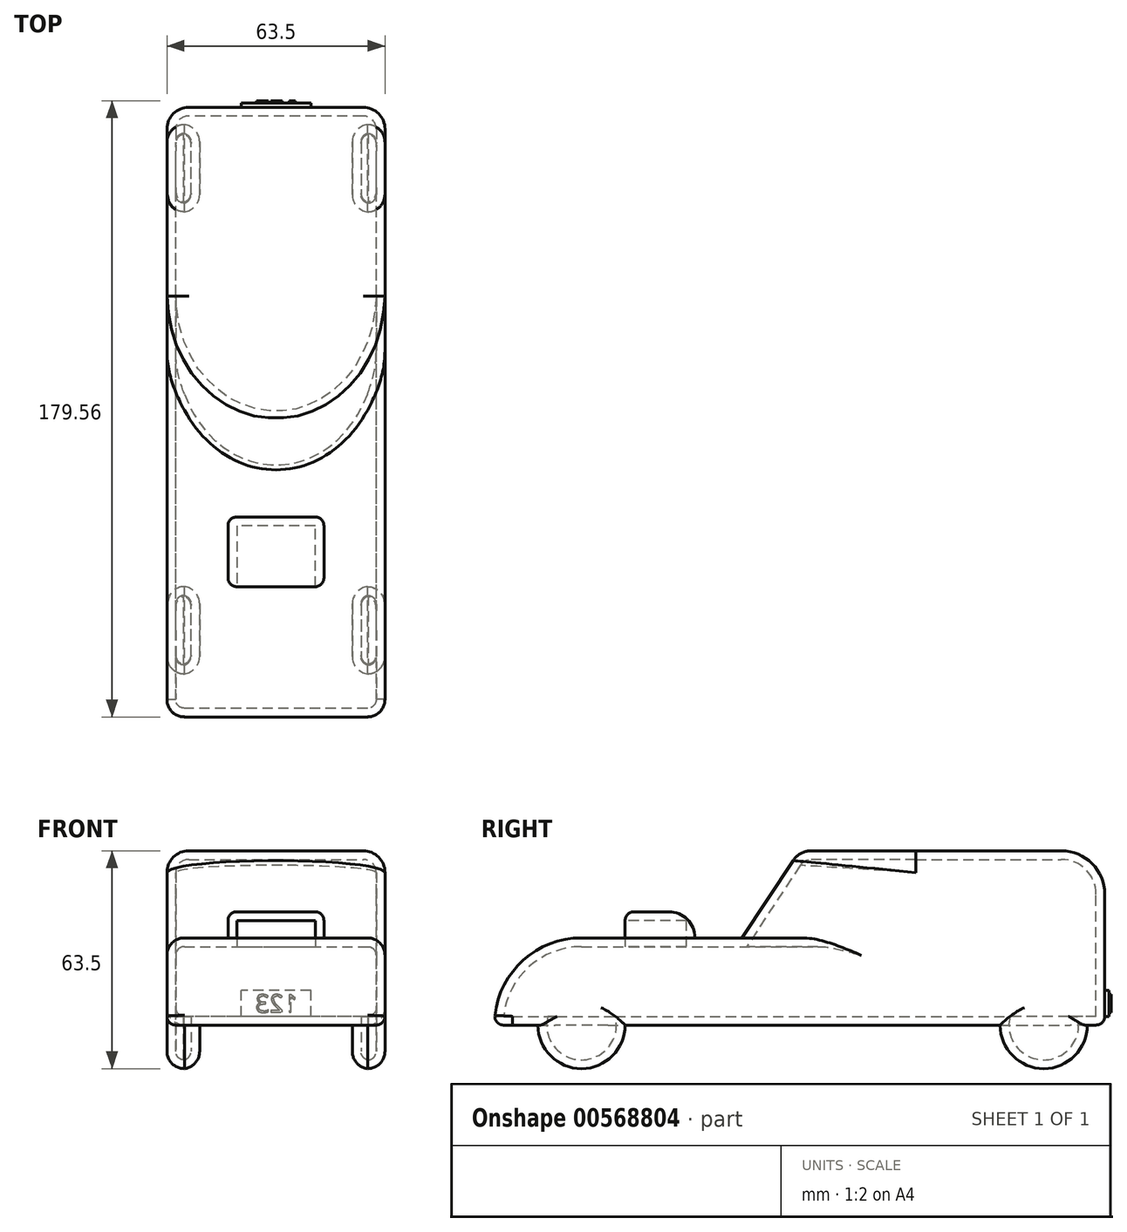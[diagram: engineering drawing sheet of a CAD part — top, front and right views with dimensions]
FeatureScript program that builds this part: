
annotation { "Feature Type Name" : "Feature", "Feature Type Description" : "" }
export const myFeature = defineFeature(function(context is Context, id is Id, definition is map)
    precondition{}
    {
        {
            var Q0;
            Q0=qCreatedBy(makeId("Right.planeOp"),FACE);
            var sketch = newSketch(context, id + "F0", { "sketchPlane" : qUnion([Q0])});
            skLineSegment(sketch, "E0", {"start": v(57.12, 17.31) * mm, "end": v(57.12, -33.49) * mm});
            skLineSegment(sketch, "E1", {"start": v(57.12, -33.49) * mm, "end": v(-69.88, -33.49) * mm});
            skLineSegment(sketch, "E2", {"start": v(-69.88, -33.49) * mm, "end": v(-69.88, -8.09) * mm});
            skLineSegment(sketch, "E3", {"start": v(-69.88, -8.09) * mm, "end": v(2.26, -8.09) * mm});
            skLineSegment(sketch, "E4", {"start": v(2.26, -8.09) * mm, "end": v(19.02, 17.31) * mm});
            skLineSegment(sketch, "E5", {"start": v(19.02, 17.31) * mm, "end": v(57.12, 17.31) * mm});
            skSolve(sketch);
        }
        {
            var Q0;
            Q0 = qSketchRegion(id + "F0", true);
            extrude(context, id + "F1", {"entities" : qUnion([Q0]), "depth" : 63.5 * mm, "offsetDistance" : 25.4 * mm});
        }
        {
            var Q0;
            Q0=makeQuery(id+"F1.opExtrude","CAP_EDGE",EDGE,{"disambiguationData":[OSD([sQuery(id+"F0.wireOp",EDGE,"E4")])],"isStart":true});
            fillet(context, id + "F2", {"entities" : qUnion([Q0]), "radius" : 31.75 * mm, "tangentPropagation" : true, "allowEdgeOverflow" : false});
        }
        {
            var Q0;
            Q0=makeQuery(id+"F1.opExtrude","CAP_EDGE",EDGE,{"disambiguationData":[OSD([sQuery(id+"F0.wireOp",EDGE,"E4")])],"isStart":false});
            fillet(context, id + "F3", {"entities" : qUnion([Q0]), "radius" : 31.75 * mm, "tangentPropagation" : true, "allowEdgeOverflow" : false});
        }
        {
            var Q0;
            Q0=makeQuery(id+"F1.opExtrude","SWEPT_EDGE",EDGE,{"disambiguationData":[OSD([sQuery(id+"F0.wireOp",EDGE,"E2"),sQuery(id+"F0.wireOp",EDGE,"E3")])]});
            fillet(context, id + "F4", {"entities" : qUnion([Q0]), "radius" : 25.4 * mm, "tangentPropagation" : true, "allowEdgeOverflow" : false});
        }
        {
            var Q0;
            Q0=makeQuery(id+"F1.opExtrude","CAP_EDGE",EDGE,{"disambiguationData":[OSD([sQuery(id+"F0.wireOp",EDGE,"E3")])],"isStart":true});
            fillet(context, id + "F5", {"entities" : qUnion([Q0]), "radius" : 5.08 * mm, "tangentPropagation" : true, "allowEdgeOverflow" : false});
        }
        {
            var Q0;
            Q0=makeQuery(id+"F1.opExtrude","CAP_EDGE",EDGE,{"disambiguationData":[OSD([sQuery(id+"F0.wireOp",EDGE,"E3")])],"isStart":false});
            fillet(context, id + "F6", {"entities" : qUnion([Q0]), "radius" : 5.08 * mm, "tangentPropagation" : true, "allowEdgeOverflow" : false});
        }
        {
            var Q0;
            Q0=makeQuery(id+"F1.opExtrude","SWEPT_FACE",FACE,{"disambiguationData":[OSD([sQuery(id+"F0.wireOp",EDGE,"E0")])]});
            extrude(context, id + "F7", {"entities" : qUnion([Q0]), "operationType" : NewBodyOperationType.ADD, "depth" : 50.8 * mm, "offsetDistance" : 25.4 * mm});
        }
        {
            var Q0;
            Q0=makeQuery(id+"F7.opExtrude","CAP_EDGE",EDGE,{"disambiguationData":[OSD([sQuery(id+"F0.wireOp",EDGE,"E0"),sQuery(id+"F0.wireOp",EDGE,"E5")])],"isStart":false});
            fillet(context, id + "F8", {"entities" : qUnion([Q0]), "radius" : 12.7 * mm, "tangentPropagation" : true, "allowEdgeOverflow" : false});
        }
        {
            var Q0;
            {var subQ0=sQuery(id+"F0.wireOp",EDGE,"E0");Q0=makeQuery(id+"F7.boolean.opBoolean","MERGE",FACE,{"derivedFrom":[makeQuery(id+"F1.opExtrude","CAP_FACE",FACE,{"disambiguationData":[OSD([subQ0,sQuery(id+"F0.wireOp",EDGE,"E1"),sQuery(id+"F0.wireOp",EDGE,"E2"),sQuery(id+"F0.wireOp",EDGE,"E3"),sQuery(id+"F0.wireOp",EDGE,"E4"),sQuery(id+"F0.wireOp",EDGE,"E5")])],"isStart":true}),makeQuery(id+"F7.opExtrude","SWEPT_FACE",FACE,{"disambiguationData":[OSD([subQ0]),TDD([makeQuery(id+"F1.opExtrude","CAP_EDGE",EDGE,{"disambiguationData":[OSD([subQ0])],"isStart":true})])]})]});}
            var sketch = newSketch(context, id + "F9", { "sketchPlane" : qUnion([Q0])});
            skCircle(sketch, "E6", {"center": v(-90.14, -33.49) * mm, "radius": 12.7 * mm});
            skCircle(sketch, "E7", {"center": v(44.48, -33.49) * mm, "radius": 12.7 * mm});
            skSolve(sketch);
        }
        {
            var Q0;
            {var subQ0=sQuery(id+"F9.wireOp",EDGE,"E6");var subQ1=sQuery(id+"F0.wireOp",EDGE,"E1");var subQ2=sQuery(id+"F0.wireOp",EDGE,"E0");var subQ3=makeQuery(id+"F7.boolean.opBoolean","MERGE",EDGE,{"derivedFrom":[makeQuery(id+"F1.opExtrude","CAP_EDGE",EDGE,{"disambiguationData":[OSD([subQ1])],"isStart":true}),makeQuery(id+"F7.opExtrude","SWEPT_EDGE",EDGE,{"disambiguationData":[OSD([subQ2,subQ1]),TDD([makeQuery(id+"F1.opExtrude","CAP_VERTEX",VERTEX,{"disambiguationData":[OSD([subQ2,subQ1])],"isStart":true})])]})]});var subQ4=makeQuery(id+"F9.imprint","INTERSECT",VERTEX,{"disambiguationData":[OD(0.0)],"derivedFrom":[subQ3,subQ0]});Q0=makeQuery(id+"F9.imprint","IMPRINT",FACE,{"disambiguationData":[TD([[makeQuery(id+"F9.imprint","IMPRINT",EDGE,{"disambiguationData":[TD([[subQ4,-1.0]])],"derivedFrom":subQ0}),1.0]])]});}
            var Q1;
            {var subQ0=sQuery(id+"F9.wireOp",EDGE,"E6");var subQ1=sQuery(id+"F0.wireOp",EDGE,"E1");var subQ2=sQuery(id+"F0.wireOp",EDGE,"E0");var subQ3=makeQuery(id+"F7.boolean.opBoolean","MERGE",EDGE,{"derivedFrom":[makeQuery(id+"F1.opExtrude","CAP_EDGE",EDGE,{"disambiguationData":[OSD([subQ1])],"isStart":true}),makeQuery(id+"F7.opExtrude","SWEPT_EDGE",EDGE,{"disambiguationData":[OSD([subQ2,subQ1]),TDD([makeQuery(id+"F1.opExtrude","CAP_VERTEX",VERTEX,{"disambiguationData":[OSD([subQ2,subQ1])],"isStart":true})])]})]});var subQ4=makeQuery(id+"F9.imprint","INTERSECT",VERTEX,{"disambiguationData":[OD(0.0)],"derivedFrom":[subQ3,subQ0]});Q1=makeQuery(id+"F9.imprint","IMPRINT",FACE,{"disambiguationData":[TD([[makeQuery(id+"F9.imprint","IMPRINT",EDGE,{"disambiguationData":[TD([[subQ4,1.0]])],"derivedFrom":subQ0}),1.0]])]});}
            var Q2;
            {var subQ0=sQuery(id+"F9.wireOp",EDGE,"E7");var subQ1=sQuery(id+"F0.wireOp",EDGE,"E1");var subQ2=sQuery(id+"F0.wireOp",EDGE,"E0");var subQ3=makeQuery(id+"F7.boolean.opBoolean","MERGE",EDGE,{"derivedFrom":[makeQuery(id+"F1.opExtrude","CAP_EDGE",EDGE,{"disambiguationData":[OSD([subQ1])],"isStart":true}),makeQuery(id+"F7.opExtrude","SWEPT_EDGE",EDGE,{"disambiguationData":[OSD([subQ2,subQ1]),TDD([makeQuery(id+"F1.opExtrude","CAP_VERTEX",VERTEX,{"disambiguationData":[OSD([subQ2,subQ1])],"isStart":true})])]})]});var subQ4=makeQuery(id+"F9.imprint","INTERSECT",VERTEX,{"disambiguationData":[OD(0.0)],"derivedFrom":[subQ3,subQ0]});Q2=makeQuery(id+"F9.imprint","IMPRINT",FACE,{"disambiguationData":[TD([[makeQuery(id+"F9.imprint","IMPRINT",EDGE,{"disambiguationData":[TD([[subQ4,-1.0]])],"derivedFrom":subQ0}),1.0]])]});}
            var Q3;
            {var subQ0=sQuery(id+"F9.wireOp",EDGE,"E7");var subQ1=sQuery(id+"F0.wireOp",EDGE,"E1");var subQ2=sQuery(id+"F0.wireOp",EDGE,"E0");var subQ3=makeQuery(id+"F7.boolean.opBoolean","MERGE",EDGE,{"derivedFrom":[makeQuery(id+"F1.opExtrude","CAP_EDGE",EDGE,{"disambiguationData":[OSD([subQ1])],"isStart":true}),makeQuery(id+"F7.opExtrude","SWEPT_EDGE",EDGE,{"disambiguationData":[OSD([subQ2,subQ1]),TDD([makeQuery(id+"F1.opExtrude","CAP_VERTEX",VERTEX,{"disambiguationData":[OSD([subQ2,subQ1])],"isStart":true})])]})]});var subQ4=makeQuery(id+"F9.imprint","INTERSECT",VERTEX,{"disambiguationData":[OD(0.0)],"derivedFrom":[subQ3,subQ0]});Q3=makeQuery(id+"F9.imprint","IMPRINT",FACE,{"disambiguationData":[TD([[makeQuery(id+"F9.imprint","IMPRINT",EDGE,{"disambiguationData":[TD([[subQ4,1.0]])],"derivedFrom":subQ0}),1.0]])]});}
            extrude(context, id + "F10", {"entities" : qUnion([Q0, Q1, Q2, Q3]), "operationType" : NewBodyOperationType.ADD, "oppositeDirection" : true, "depth" : 9.52 * mm, "offsetDistance" : 25.4 * mm});
        }
        {
            var Q0;
            {var subQ0=sQuery(id+"F0.wireOp",EDGE,"E0");Q0=makeQuery(id+"F7.boolean.opBoolean","MERGE",FACE,{"derivedFrom":[makeQuery(id+"F1.opExtrude","CAP_FACE",FACE,{"disambiguationData":[OSD([subQ0,sQuery(id+"F0.wireOp",EDGE,"E1"),sQuery(id+"F0.wireOp",EDGE,"E2"),sQuery(id+"F0.wireOp",EDGE,"E3"),sQuery(id+"F0.wireOp",EDGE,"E4"),sQuery(id+"F0.wireOp",EDGE,"E5")])],"isStart":false}),makeQuery(id+"F7.opExtrude","SWEPT_FACE",FACE,{"disambiguationData":[OSD([subQ0]),TDD([makeQuery(id+"F1.opExtrude","CAP_EDGE",EDGE,{"disambiguationData":[OSD([subQ0])],"isStart":false})])]})]});}
            var sketch = newSketch(context, id + "F11", { "sketchPlane" : qUnion([Q0])});
            skCircle(sketch, "E8", {"center": v(-44.48, -33.49) * mm, "radius": 12.7 * mm});
            skCircle(sketch, "E9", {"center": v(90.14, -33.49) * mm, "radius": 12.7 * mm});
            skSolve(sketch);
        }
        {
            var Q0;
            Q0 = qSketchRegion(id + "F11", true);
            extrude(context, id + "F12", {"entities" : qUnion([Q0]), "operationType" : NewBodyOperationType.ADD, "oppositeDirection" : true, "depth" : 9.52 * mm, "offsetDistance" : 25.4 * mm});
        }
        {
            var Q0;
            Q0=makeQuery(id+"F10.opExtrude","CAP_EDGE",EDGE,{"disambiguationData":[OSD([sQuery(id+"F9.wireOp",EDGE,"E7")])],"isStart":true});
            fillet(context, id + "F13", {"entities" : qUnion([Q0]), "radius" : 5.08 * mm, "tangentPropagation" : true, "allowEdgeOverflow" : false});
        }
        {
            var Q0;
            Q0=makeQuery(id+"F10.opExtrude","CAP_EDGE",EDGE,{"disambiguationData":[OSD([sQuery(id+"F9.wireOp",EDGE,"E7")])],"isStart":false});
            fillet(context, id + "F14", {"entities" : qUnion([Q0]), "radius" : 5.08 * mm, "tangentPropagation" : true, "allowEdgeOverflow" : false});
        }
        {
            var Q0;
            Q0=makeQuery(id+"F10.opExtrude","CAP_EDGE",EDGE,{"disambiguationData":[OSD([sQuery(id+"F9.wireOp",EDGE,"E6")])],"isStart":true});
            fillet(context, id + "F15", {"entities" : qUnion([Q0]), "radius" : 5.08 * mm, "tangentPropagation" : true, "allowEdgeOverflow" : false});
        }
        {
            var Q0;
            Q0=makeQuery(id+"F10.opExtrude","CAP_EDGE",EDGE,{"disambiguationData":[OSD([sQuery(id+"F9.wireOp",EDGE,"E6")])],"isStart":false});
            fillet(context, id + "F16", {"entities" : qUnion([Q0]), "radius" : 5.08 * mm, "tangentPropagation" : true, "allowEdgeOverflow" : false});
        }
        {
            var Q0;
            Q0=makeQuery(id+"F12.opExtrude","CAP_EDGE",EDGE,{"disambiguationData":[OSD([sQuery(id+"F11.wireOp",EDGE,"E9")])],"isStart":true});
            fillet(context, id + "F17", {"entities" : qUnion([Q0]), "radius" : 5.08 * mm, "tangentPropagation" : true, "allowEdgeOverflow" : false});
        }
        {
            var Q0;
            Q0=makeQuery(id+"F12.opExtrude","CAP_EDGE",EDGE,{"disambiguationData":[OSD([sQuery(id+"F11.wireOp",EDGE,"E8")])],"isStart":true});
            var Q1;
            Q1=makeQuery(id+"F12.opExtrude","CAP_EDGE",EDGE,{"disambiguationData":[OSD([sQuery(id+"F11.wireOp",EDGE,"E9")])],"isStart":false});
            fillet(context, id + "F18", {"entities" : qUnion([Q0, Q1]), "radius" : 5.08 * mm, "tangentPropagation" : true, "allowEdgeOverflow" : false});
        }
        {
            var Q0;
            Q0=makeQuery(id+"F12.opExtrude","CAP_EDGE",EDGE,{"disambiguationData":[OSD([sQuery(id+"F11.wireOp",EDGE,"E8")])],"isStart":false});
            fillet(context, id + "F19", {"entities" : qUnion([Q0]), "radius" : 5.08 * mm, "tangentPropagation" : true, "allowEdgeOverflow" : false});
        }
        {
            var Q0;
            Q0=makeQuery(id+"F4.opFillet","BLEND_EDGE",EDGE,{"blendedFrom":[makeQuery(id+"F1.opExtrude","SWEPT_EDGE",EDGE,{"disambiguationData":[OSD([sQuery(id+"F0.wireOp",EDGE,"E2"),sQuery(id+"F0.wireOp",EDGE,"E3")])]}),makeQuery(id+"F1.opExtrude","SWEPT_FACE",FACE,{"disambiguationData":[OSD([sQuery(id+"F0.wireOp",EDGE,"E1")])]})],"blendedInto":[makeQuery(id+"F1.opExtrude","SWEPT_FACE",FACE,{"disambiguationData":[OSD([sQuery(id+"F0.wireOp",EDGE,"E1")])]})]});
            fillet(context, id + "F20", {"entities" : qUnion([Q0]), "radius" : 2.54 * mm, "tangentPropagation" : true, "allowEdgeOverflow" : false});
        }
        {
            var Q0;
            Q0=makeQuery(id+"F2.opFillet","BLEND_EDGE",EDGE,{"blendedFrom":[makeQuery(id+"F1.opExtrude","CAP_EDGE",EDGE,{"disambiguationData":[OSD([sQuery(id+"F0.wireOp",EDGE,"E4")])],"isStart":true}),makeQuery(id+"F1.opExtrude","SWEPT_FACE",FACE,{"disambiguationData":[OSD([sQuery(id+"F0.wireOp",EDGE,"E5")])]})],"blendedInto":[makeQuery(id+"F1.opExtrude","SWEPT_FACE",FACE,{"disambiguationData":[OSD([sQuery(id+"F0.wireOp",EDGE,"E5")])]})]});
            fillet(context, id + "F21", {"entities" : qUnion([Q0]), "radius" : 6.35 * mm, "tangentPropagation" : true, "allowEdgeOverflow" : false});
        }
        {
            var Q0;
            Q0=makeQuery(id+"F7.opExtrude","CAP_EDGE",EDGE,{"disambiguationData":[OSD([sQuery(id+"F0.wireOp",EDGE,"E0"),sQuery(id+"F0.wireOp",EDGE,"E1")])],"isStart":false});
            fillet(context, id + "F22", {"entities" : qUnion([Q0]), "radius" : 2.54 * mm, "tangentPropagation" : true, "allowEdgeOverflow" : false});
        }
        {
            var Q0;
            {var subQ0=sQuery(id+"F0.wireOp",EDGE,"E1");var subQ1=sQuery(id+"F0.wireOp",EDGE,"E0");var subQ2=sQuery(id+"F9.wireOp",EDGE,"E7");var subQ3=sQuery(id+"F9.wireOp",EDGE,"E6");Q0=makeQuery(id+"F10.boolean.opBoolean","SPLIT",EDGE,{"disambiguationData":[TD([makeQuery(id+"F1.opExtrude","CAP_FACE",FACE,{"disambiguationData":[OSD([subQ1,subQ0,sQuery(id+"F0.wireOp",EDGE,"E2"),sQuery(id+"F0.wireOp",EDGE,"E3"),sQuery(id+"F0.wireOp",EDGE,"E4"),sQuery(id+"F0.wireOp",EDGE,"E5")])],"isStart":true}),makeQuery(id+"F1.opExtrude","SWEPT_FACE",FACE,{"disambiguationData":[OSD([subQ0])]}),makeQuery(id+"F7.opExtrude","SWEPT_FACE",FACE,{"disambiguationData":[OSD([subQ1,subQ0])]}),makeQuery(id+"F7.opExtrude","SWEPT_FACE",FACE,{"disambiguationData":[OSD([subQ1]),TDD([makeQuery(id+"F1.opExtrude","CAP_EDGE",EDGE,{"disambiguationData":[OSD([subQ1])],"isStart":true})])]}),makeQuery(id+"F10.opExtrude","SWEPT_FACE",FACE,{"disambiguationData":[OSD([subQ3])]}),makeQuery(id+"F10.opExtrude","CAP_FACE",FACE,{"disambiguationData":[OSD([subQ3])],"isStart":true}),makeQuery(id+"F10.opExtrude","SWEPT_FACE",FACE,{"disambiguationData":[OSD([subQ2])]}),makeQuery(id+"F10.opExtrude","CAP_FACE",FACE,{"disambiguationData":[OSD([subQ2])],"isStart":true})])],"derivedFrom":makeQuery(id+"F7.boolean.opBoolean","MERGE",EDGE,{"derivedFrom":[makeQuery(id+"F1.opExtrude","CAP_EDGE",EDGE,{"disambiguationData":[OSD([subQ0])],"isStart":true}),makeQuery(id+"F7.opExtrude","SWEPT_EDGE",EDGE,{"disambiguationData":[OSD([subQ1,subQ0]),TDD([makeQuery(id+"F1.opExtrude","CAP_VERTEX",VERTEX,{"disambiguationData":[OSD([subQ1,subQ0])],"isStart":true})])]})]})});}
            fillet(context, id + "F23", {"entities" : qUnion([Q0]), "radius" : 5.08 * mm, "tangentPropagation" : true, "allowEdgeOverflow" : false});
        }
        {
            var Q0;
            {var subQ0=sQuery(id+"F0.wireOp",EDGE,"E0");var subQ1=sQuery(id+"F11.wireOp",EDGE,"E8");var subQ2=sQuery(id+"F0.wireOp",EDGE,"E1");var subQ3=sQuery(id+"F11.wireOp",EDGE,"E9");Q0=makeQuery(id+"F12.boolean.opBoolean","SPLIT",EDGE,{"disambiguationData":[TD([makeQuery(id+"F1.opExtrude","CAP_FACE",FACE,{"disambiguationData":[OSD([subQ0,subQ2,sQuery(id+"F0.wireOp",EDGE,"E2"),sQuery(id+"F0.wireOp",EDGE,"E3"),sQuery(id+"F0.wireOp",EDGE,"E4"),sQuery(id+"F0.wireOp",EDGE,"E5")])],"isStart":false}),makeQuery(id+"F1.opExtrude","SWEPT_FACE",FACE,{"disambiguationData":[OSD([subQ2])]}),makeQuery(id+"F7.opExtrude","SWEPT_FACE",FACE,{"disambiguationData":[OSD([subQ0,subQ2])]}),makeQuery(id+"F7.opExtrude","SWEPT_FACE",FACE,{"disambiguationData":[OSD([subQ0]),TDD([makeQuery(id+"F1.opExtrude","CAP_EDGE",EDGE,{"disambiguationData":[OSD([subQ0])],"isStart":false})])]}),makeQuery(id+"F12.opExtrude","SWEPT_FACE",FACE,{"disambiguationData":[OSD([subQ1])]}),makeQuery(id+"F12.opExtrude","CAP_FACE",FACE,{"disambiguationData":[OSD([subQ1])],"isStart":true}),makeQuery(id+"F12.opExtrude","SWEPT_FACE",FACE,{"disambiguationData":[OSD([subQ3])]}),makeQuery(id+"F12.opExtrude","CAP_FACE",FACE,{"disambiguationData":[OSD([subQ3])],"isStart":true})])],"derivedFrom":makeQuery(id+"F7.boolean.opBoolean","MERGE",EDGE,{"derivedFrom":[makeQuery(id+"F1.opExtrude","CAP_EDGE",EDGE,{"disambiguationData":[OSD([subQ2])],"isStart":false}),makeQuery(id+"F7.opExtrude","SWEPT_EDGE",EDGE,{"disambiguationData":[OSD([subQ0,subQ2]),TDD([makeQuery(id+"F1.opExtrude","CAP_VERTEX",VERTEX,{"disambiguationData":[OSD([subQ0,subQ2])],"isStart":false})])]})]})});}
            fillet(context, id + "F24", {"entities" : qUnion([Q0]), "radius" : 5.08 * mm, "tangentPropagation" : true, "allowEdgeOverflow" : false});
        }
        {
            var Q0;
            Q0=makeQuery(id+"F1.opExtrude","SWEPT_FACE",FACE,{"disambiguationData":[OSD([sQuery(id+"F0.wireOp",EDGE,"E3")])]});
            var sketch = newSketch(context, id + "F25", { "sketchPlane" : qUnion([Q0])});
            skLineSegment(sketch, "E10", {"start": v(17.78, -11.46) * mm, "end": v(17.78, -31.78) * mm});
            skLineSegment(sketch, "E11", {"start": v(17.78, -31.78) * mm, "end": v(45.72, -31.78) * mm});
            skLineSegment(sketch, "E12", {"start": v(45.72, -31.78) * mm, "end": v(45.72, -11.46) * mm});
            skLineSegment(sketch, "E13", {"start": v(45.72, -11.46) * mm, "end": v(17.78, -11.46) * mm});
            skSolve(sketch);
        }
        {
            var Q0;
            Q0=makeQuery(id+"F25.imprint","IMPRINT",FACE,{"disambiguationData":[TD([[makeQuery(id+"F25.imprint","IMPRINT",EDGE,{"derivedFrom":sQuery(id+"F25.wireOp",EDGE,"E10")}),1.0]])]});
            extrude(context, id + "F26", {"entities" : qUnion([Q0]), "operationType" : NewBodyOperationType.ADD, "depth" : 7.62 * mm, "offsetDistance" : 25.4 * mm});
        }
        {
            var Q0;
            Q0=makeQuery(id+"F26.opExtrude","SWEPT_FACE",FACE,{"disambiguationData":[OSD([sQuery(id+"F25.wireOp",EDGE,"E11")])]});
            shell(context, id + "F27", {"entities" : qUnion([Q0]), "thickness" : 2.54 * mm});
        }
        {
            var Q0;
            Q0=makeQuery(id+"F26.opExtrude","CAP_EDGE",EDGE,{"disambiguationData":[OSD([sQuery(id+"F25.wireOp",EDGE,"E13")])],"isStart":false});
            fillet(context, id + "F28", {"entities" : qUnion([Q0]), "radius" : 7.62 * mm, "tangentPropagation" : true, "allowEdgeOverflow" : false});
        }
        {
            var Q0;
            Q0=makeQuery(id+"F26.opExtrude","CAP_EDGE",EDGE,{"disambiguationData":[OSD([sQuery(id+"F25.wireOp",EDGE,"E10")])],"isStart":false});
            fillet(context, id + "F29", {"entities" : qUnion([Q0]), "radius" : 2.54 * mm, "tangentPropagation" : true, "allowEdgeOverflow" : false});
        }
        {
            var Q0;
            Q0=makeQuery(id+"F26.opExtrude","CAP_EDGE",EDGE,{"disambiguationData":[OSD([sQuery(id+"F25.wireOp",EDGE,"E12")])],"isStart":false});
            fillet(context, id + "F30", {"entities" : qUnion([Q0]), "radius" : 2.54 * mm, "tangentPropagation" : true, "allowEdgeOverflow" : false});
        }
        {
            var Q0;
            Q0=makeQuery(id+"F26.opExtrude","SWEPT_EDGE",EDGE,{"disambiguationData":[OSD([sQuery(id+"F25.wireOp",EDGE,"E11"),sQuery(id+"F25.wireOp",EDGE,"E12")])]});
            var Q1;
            Q1=makeQuery(id+"F26.opExtrude","CAP_EDGE",EDGE,{"disambiguationData":[OSD([sQuery(id+"F25.wireOp",EDGE,"E11")])],"isStart":false});
            var Q2;
            Q2=makeQuery(id+"F30.opFillet","BLEND_EDGE",EDGE,{"blendedFrom":[makeQuery(id+"F26.opExtrude","CAP_EDGE",EDGE,{"disambiguationData":[OSD([sQuery(id+"F25.wireOp",EDGE,"E12")])],"isStart":false}),makeQuery(id+"F26.opExtrude","SWEPT_FACE",FACE,{"disambiguationData":[OSD([sQuery(id+"F25.wireOp",EDGE,"E11")])]})],"blendedInto":[makeQuery(id+"F26.opExtrude","SWEPT_FACE",FACE,{"disambiguationData":[OSD([sQuery(id+"F25.wireOp",EDGE,"E11")])]})]});
            var Q3;
            Q3=makeQuery(id+"F29.opFillet","BLEND_EDGE",EDGE,{"blendedFrom":[makeQuery(id+"F26.opExtrude","CAP_EDGE",EDGE,{"disambiguationData":[OSD([sQuery(id+"F25.wireOp",EDGE,"E10")])],"isStart":false}),makeQuery(id+"F26.opExtrude","SWEPT_FACE",FACE,{"disambiguationData":[OSD([sQuery(id+"F25.wireOp",EDGE,"E11")])]})],"blendedInto":[makeQuery(id+"F26.opExtrude","SWEPT_FACE",FACE,{"disambiguationData":[OSD([sQuery(id+"F25.wireOp",EDGE,"E11")])]})]});
            var Q4;
            Q4=makeQuery(id+"F26.opExtrude","SWEPT_EDGE",EDGE,{"disambiguationData":[OSD([sQuery(id+"F25.wireOp",EDGE,"E10"),sQuery(id+"F25.wireOp",EDGE,"E11")])]});
            fillet(context, id + "F31", {"entities" : qUnion([Q0, Q1, Q2, Q3, Q4]), "radius" : 2.54 * mm, "tangentPropagation" : true, "allowEdgeOverflow" : false});
        }
        {
            var Q0;
            Q0=makeQuery(id+"F7.opExtrude","CAP_FACE",FACE,{"disambiguationData":[OSD([sQuery(id+"F0.wireOp",EDGE,"E0")])],"isStart":false});
            var sketch = newSketch(context, id + "F32", { "sketchPlane" : qUnion([Q0])});
            skLineSegment(sketch, "E14.bottom", {"start": v(-41.91, -30.95) * mm, "end": v(-21.59, -30.95) * mm});
            skLineSegment(sketch, "E14.top", {"start": v(-41.91, -23.33) * mm, "end": v(-21.59, -23.33) * mm});
            skLineSegment(sketch, "E14.left", {"start": v(-41.91, -30.95) * mm, "end": v(-41.91, -23.33) * mm});
            skLineSegment(sketch, "E14.right", {"start": v(-21.59, -30.95) * mm, "end": v(-21.59, -23.33) * mm});
            skSolve(sketch);
        }
        {
            var Q0;
            Q0=makeQuery(id+"F32.imprint","IMPRINT",FACE,{"disambiguationData":[TD([[makeQuery(id+"F32.imprint","IMPRINT",EDGE,{"derivedFrom":sQuery(id+"F32.wireOp",EDGE,"E14.bottom")}),1.0]])]});
            extrude(context, id + "F33", {"entities" : qUnion([Q0]), "operationType" : NewBodyOperationType.ADD, "depth" : 1.27 * mm, "offsetDistance" : 25.4 * mm});
        }
        {
            var Q0;
            Q0=makeQuery(id+"F33.opExtrude","CAP_FACE",FACE,{"disambiguationData":[OSD([sQuery(id+"F32.wireOp",EDGE,"E14.bottom"),sQuery(id+"F32.wireOp",EDGE,"E14.top"),sQuery(id+"F32.wireOp",EDGE,"E14.left"),sQuery(id+"F32.wireOp",EDGE,"E14.right")])],"isStart":false});
            var sketch = newSketch(context, id + "F34", { "sketchPlane" : qUnion([Q0])});
            skText(sketch, "E15", { "text": "123\n", "fontName": "OpenSans-Regular.ttf"});
            const initialGuessF34  = {"E15": [-0.03809, -0.02978, 1, 0, 0.0052]};
            skSetInitialGuess(sketch, initialGuessF34);
            skSolve(sketch);
        }
        {
            var Q0;
            Q0 = qSketchRegion(id + "F34", true);
            extrude(context, id + "F35", {"entities" : qUnion([Q0]), "operationType" : NewBodyOperationType.ADD, "depth" : 0.64 * mm, "offsetDistance" : 25.4 * mm});
        }
    });
